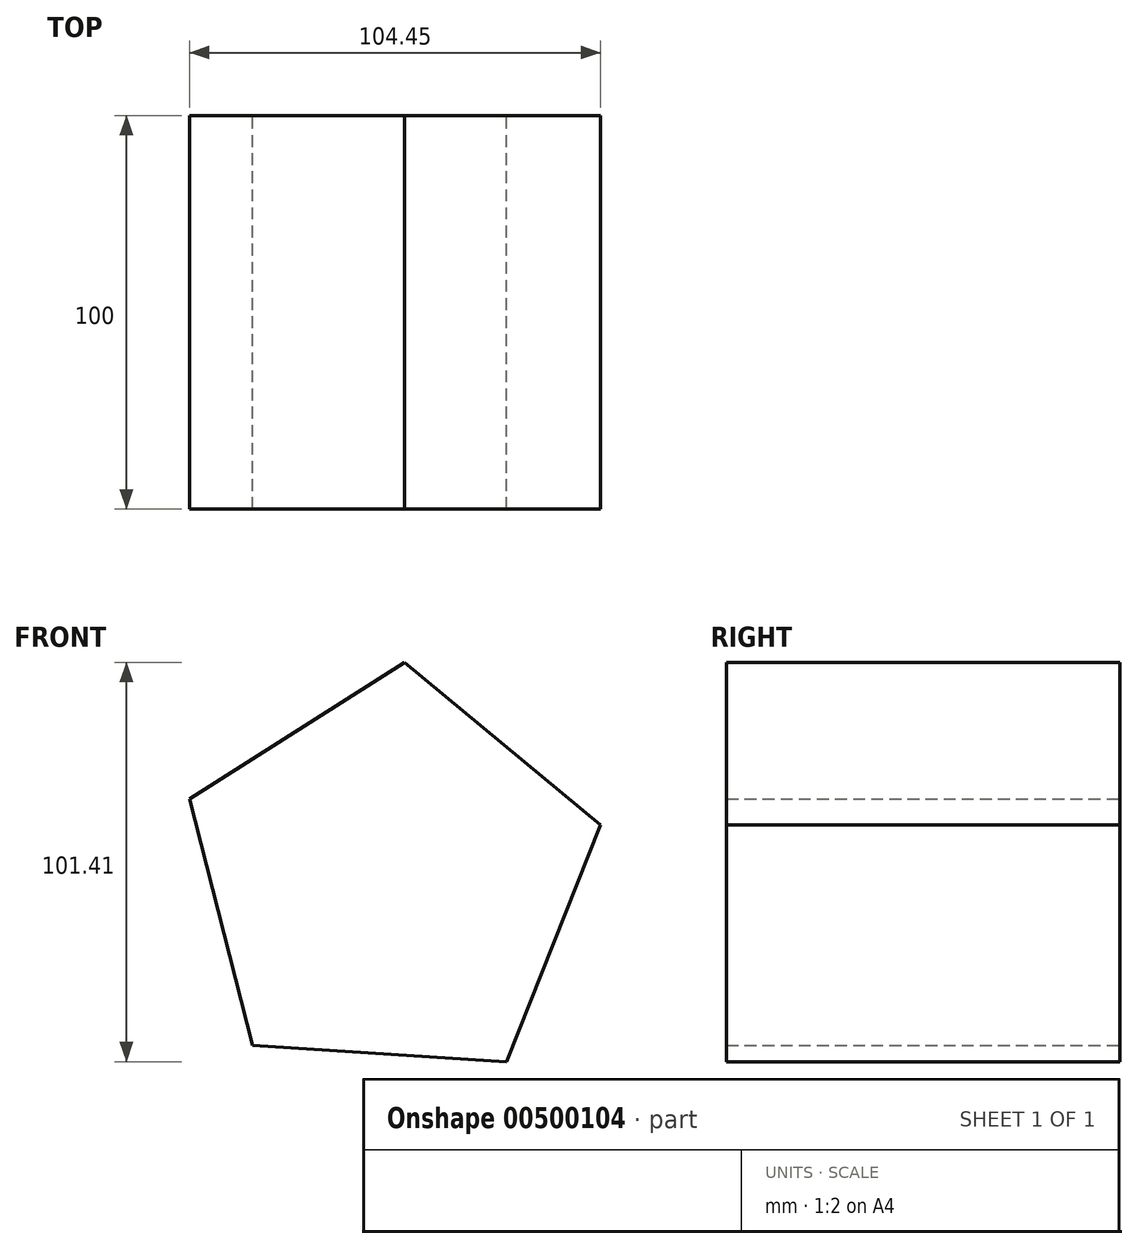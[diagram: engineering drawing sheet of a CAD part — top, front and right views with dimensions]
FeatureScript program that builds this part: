
annotation { "Feature Type Name" : "Feature", "Feature Type Description" : "" }
export const myFeature = defineFeature(function(context is Context, id is Id, definition is map)
    precondition{}
    {
        {
            var Q0;
            Q0=qCreatedBy(makeId("Front.planeOp"),FACE);
            var sketch = newSketch(context, id + "F0", { "sketchPlane" : qUnion([Q0])});
            skCircle(sketch, "E0.cCircle", {"center": v(0, 0) * mm, "radius": 55.03 * mm, "construction": true});
            skLineSegment(sketch, "E0.0", {"start": v(29.44, -46.5) * mm, "end": v(-35.12, -42.36) * mm});
            skLineSegment(sketch, "E0.1", {"start": v(-35.12, -42.36) * mm, "end": v(-51.14, 20.3) * mm});
            skLineSegment(sketch, "E0.2", {"start": v(-51.14, 20.3) * mm, "end": v(3.5, 54.92) * mm});
            skLineSegment(sketch, "E0.3", {"start": v(3.5, 54.92) * mm, "end": v(53.31, 13.63) * mm});
            skLineSegment(sketch, "E0.4", {"start": v(53.31, 13.63) * mm, "end": v(29.44, -46.5) * mm});
            skSolve(sketch);
        }
        {
            var Q0;
            Q0 = qSketchRegion(id + "F0", true);
            extrude(context, id + "F1", {"entities" : qUnion([Q0]), "endBound" : BoundingType.SYMMETRIC, "depth" : 100 * mm});
        }
    });
